# Revit family: Wing E150AC
name_source: partatom
category: Mechanical Equipment
revit_build: Autodesk Revit 2017 (Build: 20160720_1515(x64)
units: mm (PartAtom-declared; Revit-internal decimal feet)

## family parameters
Cut with Voids When Loaded = No
Host = Face
OmniClass Number = 23.75.70.21.17
OmniClass Title = Air Curtains
Part Type = Normal
Room Calculation Point = No
Round Connector Dimension = Use Diameter
Shared = No

## types (3) — shared parameters
Default Elevation = 1 m
Electric heat power for 3 ~ 400/50 = 12 kW
Electrical Potential = 400 V
Frequency = 50 Hz
Heater frequency = 50 Hz
Heater power supply = 400 V
Manufacturer = VTS
Model = WING E150AC
Motor rated current AC = 2 A
Protection rating AC = 20
URL = http://vtsgroup.com
W = 2 m
Weight = 37.00 kg
zero-valued in all types: a

## per-type parameters (varying)
| type | FAN speed | Fan output | Horizontal range |
| WING E150AC HIGH | HIGH | 3150.0 m³/h | 4 m |
| WING E150AC MEDIUM | MEDIUM | 2050.0 m³/h | 3 m |
| WING E150AC LOW | LOW | 1450.0 m³/h | 2 m |

## geometry (parser evidence)
native form markers: Sweep x7
no freeform markers — native parametric forms only
